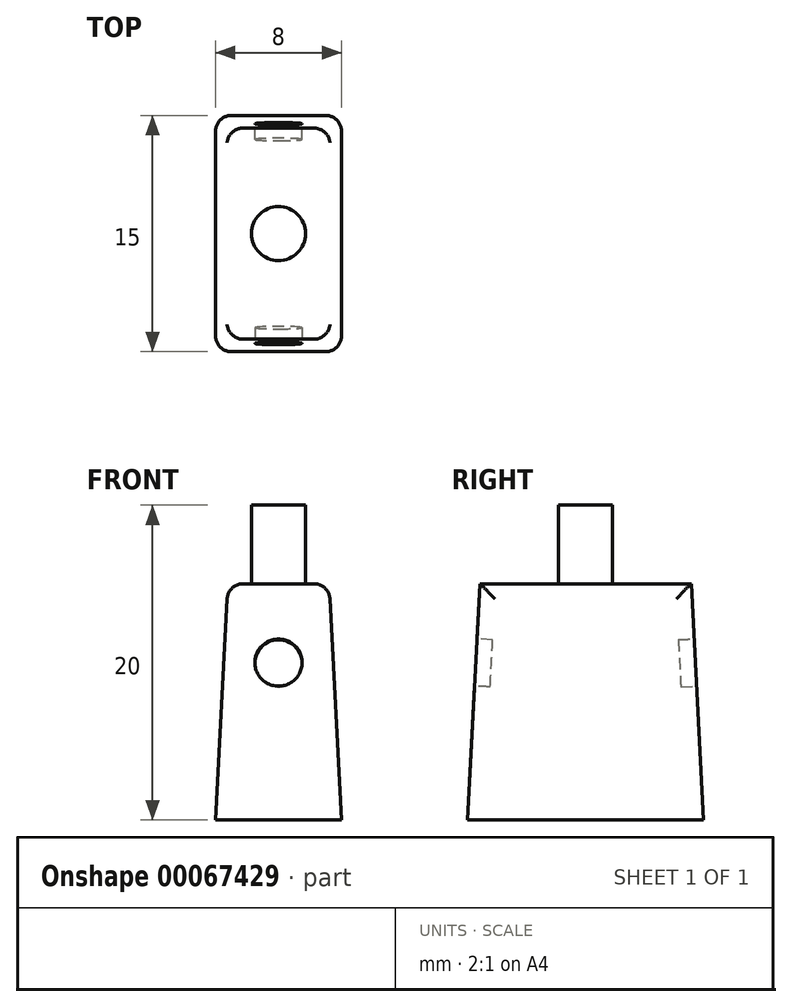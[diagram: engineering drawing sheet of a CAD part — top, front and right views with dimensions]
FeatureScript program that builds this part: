
annotation { "Feature Type Name" : "Feature", "Feature Type Description" : "" }
export const myFeature = defineFeature(function(context is Context, id is Id, definition is map)
    precondition{}
    {
        {
            var Q0;
            Q0=qCreatedBy(makeId("Top.planeOp"),FACE);
            var sketch = newSketch(context, id + "F0", { "sketchPlane" : qUnion([Q0])});
            skLineSegment(sketch, "E0.rect.bottom", {"start": v(-4, 7.5) * mm, "end": v(4, 7.5) * mm});
            skLineSegment(sketch, "E0.rect.top", {"start": v(-4, -7.5) * mm, "end": v(4, -7.5) * mm});
            skLineSegment(sketch, "E0.rect.left", {"start": v(-4, 7.5) * mm, "end": v(-4, -7.5) * mm});
            skLineSegment(sketch, "E0.rect.right", {"start": v(4, 7.5) * mm, "end": v(4, -7.5) * mm});
            skPoint(sketch, "E0.rect.middle", {"position": v(0, 0) * mm});
            skSolve(sketch);
        }
        {
            var Q0;
            Q0 = qSketchRegion(id + "F0", true);
            extrude(context, id + "F1", {"entities" : qUnion([Q0]), "depth" : 15 * mm, "hasDraft" : true, "draftAngle" : 3 * degree, "draftPullDirection" : true});
        }
        {
            var Q0;
            Q0=makeQuery(id+"F1.opExtrude","CAP_FACE",FACE,{"disambiguationData":[OSD([sQuery(id+"F0.wireOp",EDGE,"E0.rect.bottom"),sQuery(id+"F0.wireOp",EDGE,"E0.rect.top"),sQuery(id+"F0.wireOp",EDGE,"E0.rect.left"),sQuery(id+"F0.wireOp",EDGE,"E0.rect.right")])],"isStart":false});
            var sketch = newSketch(context, id + "F2", { "sketchPlane" : qUnion([Q0])});
            skCircle(sketch, "E1", {"center": v(0, 0) * mm, "radius": 1.71 * mm});
            skSolve(sketch);
        }
        {
            var Q0;
            Q0 = qSketchRegion(id + "F2", true);
            extrude(context, id + "F3", {"entities" : qUnion([Q0]), "operationType" : NewBodyOperationType.ADD, "depth" : 5 * mm});
        }
        {
            var Q0;
            Q0=makeQuery(id+"F1.opExtrude","SWEPT_FACE",FACE,{"disambiguationData":[OSD([sQuery(id+"F0.wireOp",EDGE,"E0.rect.bottom")])]});
            var sketch = newSketch(context, id + "F4", { "sketchPlane" : qUnion([Q0])});
            skCircle(sketch, "E2", {"center": v(0, 9.63) * mm, "radius": 1.5 * mm});
            skSolve(sketch);
        }
        {
            var Q0;
            Q0=makeQuery(id+"F4.imprint","IMPRINT",FACE,{"disambiguationData":[TD([[makeQuery(id+"F4.imprint","IMPRINT",EDGE,{"derivedFrom":sQuery(id+"F4.wireOp",EDGE,"E2")}),1.0]])]});
            extrude(context, id + "F5", {"entities" : qUnion([Q0]), "operationType" : NewBodyOperationType.REMOVE, "oppositeDirection" : true, "depth" : 1 * mm});
        }
        {
            var Q0;
            Q0=makeQuery(id+"F1.opExtrude","SWEPT_FACE",FACE,{"disambiguationData":[OSD([sQuery(id+"F0.wireOp",EDGE,"E0.rect.top")])]});
            var sketch = newSketch(context, id + "F6", { "sketchPlane" : qUnion([Q0])});
            skCircle(sketch, "E3", {"center": v(0, 9.63) * mm, "radius": 1.5 * mm});
            skSolve(sketch);
        }
        {
            var Q0;
            Q0 = qSketchRegion(id + "F6", true);
            extrude(context, id + "F7", {"entities" : qUnion([Q0]), "operationType" : NewBodyOperationType.REMOVE, "oppositeDirection" : true, "depth" : 1 * mm});
        }
        {
            var Q0;
            Q0=makeQuery(id+"F1.opExtrude","CAP_EDGE",EDGE,{"disambiguationData":[OSD([sQuery(id+"F0.wireOp",EDGE,"E0.rect.left")])],"isStart":false});
            var Q1;
            Q1=makeQuery(id+"F1.opExtrude","SWEPT_EDGE",EDGE,{"disambiguationData":[OSD([sQuery(id+"F0.wireOp",EDGE,"E0.rect.bottom"),sQuery(id+"F0.wireOp",EDGE,"E0.rect.left")])]});
            var Q2;
            Q2=makeQuery(id+"F1.opExtrude","SWEPT_EDGE",EDGE,{"disambiguationData":[OSD([sQuery(id+"F0.wireOp",EDGE,"E0.rect.top"),sQuery(id+"F0.wireOp",EDGE,"E0.rect.left")])]});
            var Q3;
            Q3=makeQuery(id+"F1.opExtrude","CAP_EDGE",EDGE,{"disambiguationData":[OSD([sQuery(id+"F0.wireOp",EDGE,"E0.rect.right")])],"isStart":false});
            var Q4;
            Q4=makeQuery(id+"F1.opExtrude","SWEPT_EDGE",EDGE,{"disambiguationData":[OSD([sQuery(id+"F0.wireOp",EDGE,"E0.rect.top"),sQuery(id+"F0.wireOp",EDGE,"E0.rect.right")])]});
            var Q5;
            Q5=makeQuery(id+"F1.opExtrude","SWEPT_EDGE",EDGE,{"disambiguationData":[OSD([sQuery(id+"F0.wireOp",EDGE,"E0.rect.bottom"),sQuery(id+"F0.wireOp",EDGE,"E0.rect.right")])]});
            fillet(context, id + "F8", {"entities" : qUnion([Q0, Q1, Q2, Q3, Q4, Q5]), "radius" : 1 * mm, "tangentPropagation" : true, "allowEdgeOverflow" : false});
        }
    });
